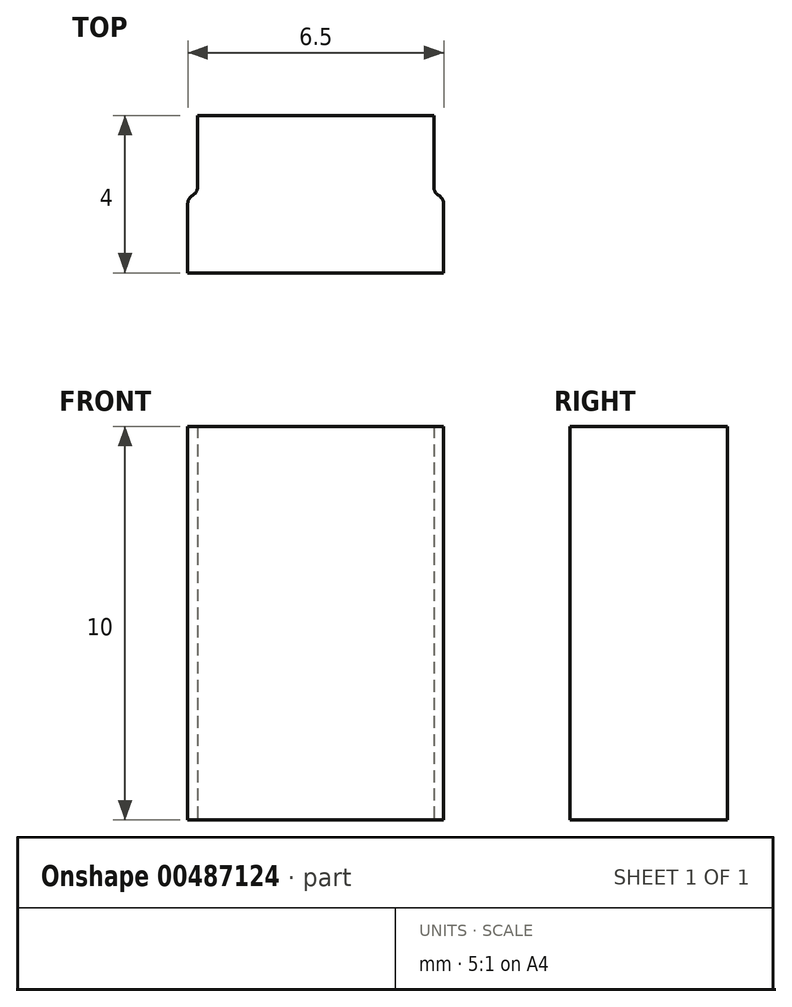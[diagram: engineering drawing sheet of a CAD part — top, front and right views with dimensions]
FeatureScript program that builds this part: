
annotation { "Feature Type Name" : "Feature", "Feature Type Description" : "" }
export const myFeature = defineFeature(function(context is Context, id is Id, definition is map)
    precondition{}
    {
        {
            var Q0;
            Q0=qCreatedBy(makeId("Top.planeOp"),FACE);
            var sketch = newSketch(context, id + "F0", { "sketchPlane" : qUnion([Q0])});
            skLineSegment(sketch, "E0", {"start": v(-10.4, 7.7) * mm, "end": v(-10.4, 9.7) * mm});
            skLineSegment(sketch, "E1", {"start": v(-10.4, 9.7) * mm, "end": v(-16.4, 9.7) * mm});
            skLineSegment(sketch, "E2", {"start": v(-16.4, 9.7) * mm, "end": v(-16.4, 7.7) * mm});
            skLineSegment(sketch, "E3", {"start": v(-16.4, 5.7) * mm, "end": v(-10.4, 5.7) * mm});
            skLineSegment(sketch, "E4", {"start": v(-13.4, 5.7) * mm, "end": v(-10.15, 5.7) * mm});
            skLineSegment(sketch, "E5", {"start": v(-10.15, 5.7) * mm, "end": v(-10.15, 7.7) * mm});
            skLineSegment(sketch, "E6", {"start": v(-10.15, 7.7) * mm, "end": v(-10.4, 7.7) * mm});
            skLineSegment(sketch, "E7", {"start": v(-16.4, 7.7) * mm, "end": v(-16.65, 7.7) * mm});
            skLineSegment(sketch, "E8", {"start": v(-16.65, 7.7) * mm, "end": v(-16.65, 5.7) * mm});
            skLineSegment(sketch, "E9", {"start": v(-16.65, 5.7) * mm, "end": v(-16.4, 5.7) * mm});
            skSolve(sketch);
        }
        {
            var Q0;
            Q0 = qSketchRegion(id + "F0", true);
            extrude(context, id + "F1", {"entities" : qUnion([Q0]), "depth" : 10 * mm});
        }
        {
            var Q0;
            Q0=makeQuery(id+"F1.opExtrude","SWEPT_EDGE",EDGE,{"disambiguationData":[OSD([sQuery(id+"F0.wireOp",EDGE,"E5"),sQuery(id+"F0.wireOp",EDGE,"E6")])]});
            var Q1;
            Q1=makeQuery(id+"F1.opExtrude","SWEPT_EDGE",EDGE,{"disambiguationData":[OSD([sQuery(id+"F0.wireOp",EDGE,"E7"),sQuery(id+"F0.wireOp",EDGE,"E8")])]});
            fillet(context, id + "F2", {"entities" : qUnion([Q0, Q1]), "radius" : 0.25 * mm, "tangentPropagation" : true, "allowEdgeOverflow" : false});
        }
        {
            var Q0;
            Q0=makeQuery(id+"F2.opFillet","BLEND_EDGE",EDGE,{"blendedFrom":[makeQuery(id+"F1.opExtrude","SWEPT_EDGE",EDGE,{"disambiguationData":[OSD([sQuery(id+"F0.wireOp",EDGE,"E7"),sQuery(id+"F0.wireOp",EDGE,"E8")])]}),makeQuery(id+"F1.opExtrude","SWEPT_FACE",FACE,{"disambiguationData":[OSD([sQuery(id+"F0.wireOp",EDGE,"E2")])]})],"blendedInto":[makeQuery(id+"F1.opExtrude","SWEPT_FACE",FACE,{"disambiguationData":[OSD([sQuery(id+"F0.wireOp",EDGE,"E2")])]})]});
            var Q1;
            Q1=makeQuery(id+"F2.opFillet","BLEND_EDGE",EDGE,{"blendedFrom":[makeQuery(id+"F1.opExtrude","SWEPT_EDGE",EDGE,{"disambiguationData":[OSD([sQuery(id+"F0.wireOp",EDGE,"E5"),sQuery(id+"F0.wireOp",EDGE,"E6")])]}),makeQuery(id+"F1.opExtrude","SWEPT_FACE",FACE,{"disambiguationData":[OSD([sQuery(id+"F0.wireOp",EDGE,"E0")])]})],"blendedInto":[makeQuery(id+"F1.opExtrude","SWEPT_FACE",FACE,{"disambiguationData":[OSD([sQuery(id+"F0.wireOp",EDGE,"E0")])]})]});
            fillet(context, id + "F3", {"entities" : qUnion([Q0, Q1]), "radius" : 0.25 * mm, "tangentPropagation" : true, "allowEdgeOverflow" : false});
        }
    });
